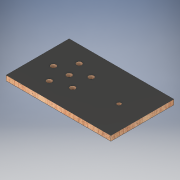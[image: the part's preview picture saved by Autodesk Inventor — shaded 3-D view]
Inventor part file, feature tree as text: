
AUTODESK INVENTOR PART (.ipt)
format: ipt  version: 2017 (Build 210142000, 142)  size: 145,408 bytes
history: native  units: in
note: dims shown in document units (in); Inventor stores cm internally (conversion verified against a paired STEP export)
features: extrude x2, sketch x2
ambient origin geometry x8: Origin, YZ Plane, XZ Plane, XY Plane, X Axis, Y Axis, Z Axis, Center Point
bodies: Solid1 (feature_tree)
feature tree (4):
  extrude  "Extrusion1"  Depth=9.9688in
  extrude  "Extrusion2"  Depth=0.4688in
  sketch  "Sketch1"  dims[d0=6.0in d1=9.9688in]
  sketch  "Sketch2"  dims[d2=2.2188in d3=0.375in d4=0.4688in d5=0.0in d6=0.5in d7=1.5in d8=0.5in d9=1.9685in d11=360.0deg d13=6.9688in d14=0.4688in d15=0.0in]
